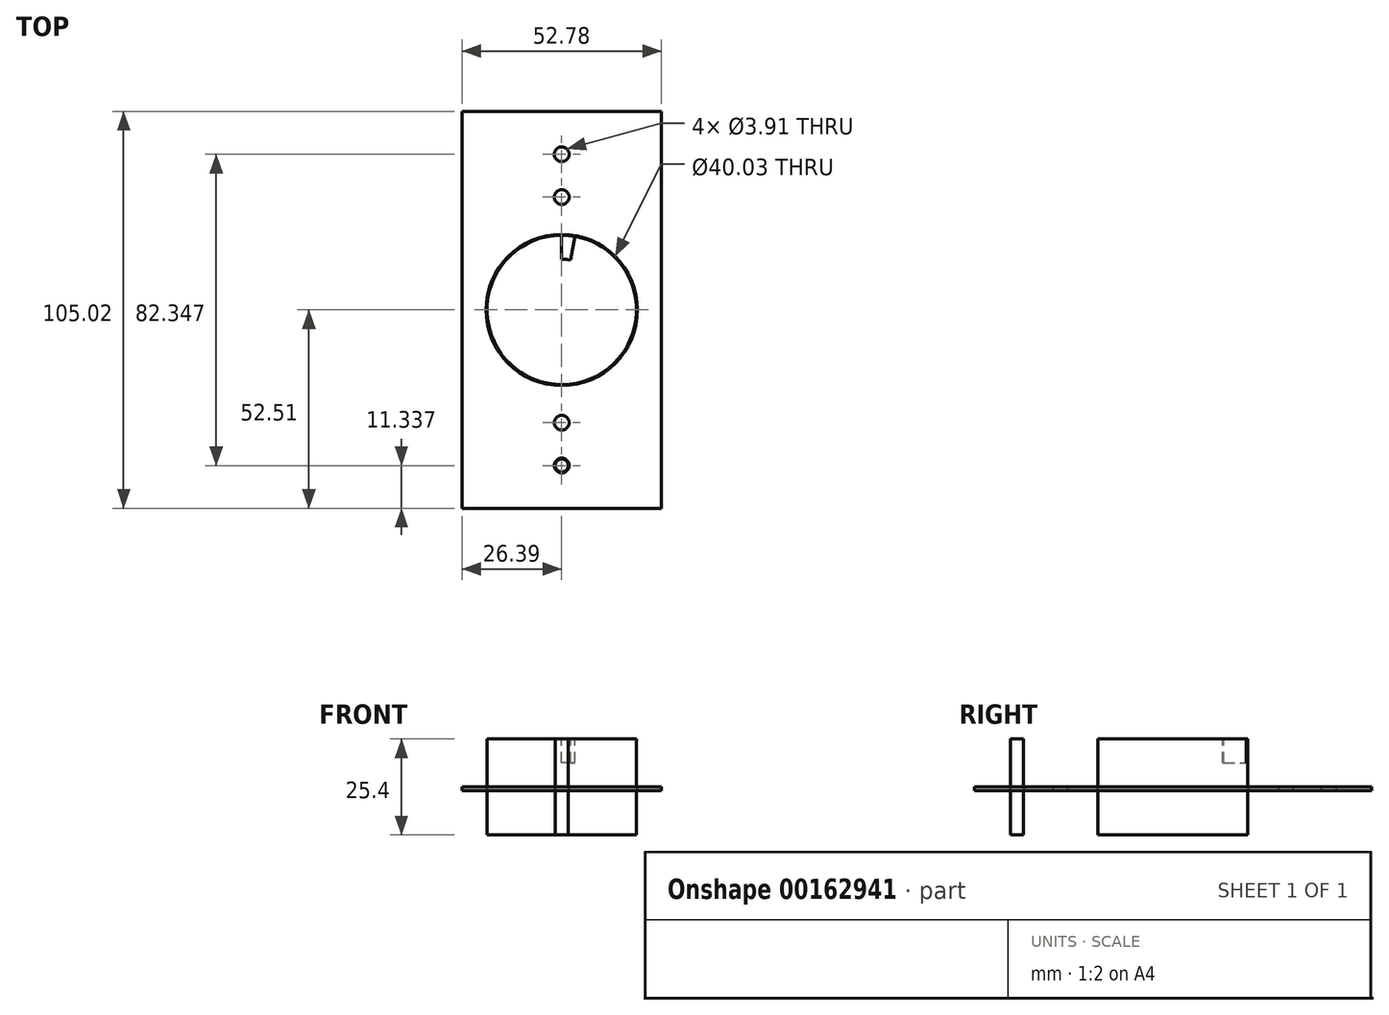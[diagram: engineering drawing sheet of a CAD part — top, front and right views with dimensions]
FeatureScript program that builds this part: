
annotation { "Feature Type Name" : "Feature", "Feature Type Description" : "" }
export const myFeature = defineFeature(function(context is Context, id is Id, definition is map)
    precondition{}
    {
        {
            var Q0;
            Q0=qCreatedBy(makeId("Top.planeOp"),FACE);
            var sketch = newSketch(context, id + "F0", { "sketchPlane" : qUnion([Q0])});
            skLineSegment(sketch, "E0.bottom", {"start": v(-26.4, 52.51) * mm, "end": v(26.4, 52.51) * mm});
            skLineSegment(sketch, "E0.top", {"start": v(-26.4, -52.51) * mm, "end": v(26.4, -52.51) * mm});
            skLineSegment(sketch, "E0.left", {"start": v(-26.4, 52.51) * mm, "end": v(-26.4, -52.51) * mm});
            skLineSegment(sketch, "E0.right", {"start": v(26.4, 52.51) * mm, "end": v(26.4, -52.51) * mm});
            skPoint(sketch, "E1", {"position": v(26.4, 0) * mm});
            skPoint(sketch, "E2", {"position": v(0, 52.51) * mm});
            skCircle(sketch, "E3", {"center": v(0, 0) * mm, "radius": 20.02 * mm});
            skCircle(sketch, "E4", {"center": v(0, 29.85) * mm, "radius": 1.96 * mm});
            skCircle(sketch, "E5", {"center": v(0, 41.17) * mm, "radius": 1.96 * mm});
            skLineSegment(sketch, "E6", {"start": v(26.4, 0) * mm, "end": v(-26.4, 0) * mm, "construction": true});
            skCircle(sketch, "E7.MirrorC", {"center": v(0, -41.17) * mm, "radius": 1.96 * mm});
            skCircle(sketch, "E8.MirrorC", {"center": v(0, -29.85) * mm, "radius": 1.96 * mm});
            skSolve(sketch);
        }
        {
            var Q0;
            Q0=makeQuery(id+"F0.imprint","IMPRINT",FACE,{"disambiguationData":[TD([[makeQuery(id+"F0.imprint","IMPRINT",EDGE,{"derivedFrom":sQuery(id+"F0.wireOp",EDGE,"E0.bottom")}),-1.0]])]});
            extrude(context, id + "F1", {"entities" : qUnion([Q0]), "depth" : 1.04 * mm});
        }
        {
            var Q0;
            Q0=makeQuery(id+"F1.opExtrude","CAP_FACE",FACE,{"disambiguationData":[OSD([sQuery(id+"F0.wireOp",EDGE,"E0.bottom"),sQuery(id+"F0.wireOp",EDGE,"E0.top"),sQuery(id+"F0.wireOp",EDGE,"E0.left"),sQuery(id+"F0.wireOp",EDGE,"E0.right"),sQuery(id+"F0.wireOp",EDGE,"E3"),sQuery(id+"F0.wireOp",EDGE,"E4"),sQuery(id+"F0.wireOp",EDGE,"E5"),sQuery(id+"F0.wireOp",EDGE,"E7.MirrorC"),sQuery(id+"F0.wireOp",EDGE,"E8.MirrorC")])],"isStart":false});
            var sketch = newSketch(context, id + "F2", { "sketchPlane" : qUnion([Q0])});
            skCircle(sketch, "E9", {"center": v(0, 0) * mm, "radius": 19.76 * mm});
            skSolve(sketch);
        }
        {
            var Q0;
            Q0 = qSketchRegion(id + "F2", true);
            extrude(context, id + "F3", {"entities" : qUnion([Q0]), "endBound" : BoundingType.SYMMETRIC, "depth" : 25.4 * mm});
        }
        {
            var Q0;
            Q0=makeQuery(id+"F1.opExtrude","CAP_FACE",FACE,{"disambiguationData":[OSD([sQuery(id+"F0.wireOp",EDGE,"E0.bottom"),sQuery(id+"F0.wireOp",EDGE,"E0.top"),sQuery(id+"F0.wireOp",EDGE,"E0.left"),sQuery(id+"F0.wireOp",EDGE,"E0.right"),sQuery(id+"F0.wireOp",EDGE,"E3"),sQuery(id+"F0.wireOp",EDGE,"E4"),sQuery(id+"F0.wireOp",EDGE,"E5"),sQuery(id+"F0.wireOp",EDGE,"E7.MirrorC"),sQuery(id+"F0.wireOp",EDGE,"E8.MirrorC")])],"isStart":false});
            var sketch = newSketch(context, id + "F4", { "sketchPlane" : qUnion([Q0])});
            skCircle(sketch, "E10", {"center": v(0, -41.17) * mm, "radius": 1.7 * mm});
            skSolve(sketch);
        }
        {
            var Q0;
            Q0=makeQuery(id+"F4.imprint","IMPRINT",FACE,{"disambiguationData":[TD([[makeQuery(id+"F4.imprint","IMPRINT",EDGE,{"derivedFrom":sQuery(id+"F4.wireOp",EDGE,"E10")}),1.0]])]});
            extrude(context, id + "F5", {"entities" : qUnion([Q0]), "endBound" : BoundingType.SYMMETRIC, "depth" : 25.4 * mm});
        }
        {
            var Q0;
            Q0=makeQuery(id+"F3.opExtrude","CAP_FACE",FACE,{"disambiguationData":[OSD([sQuery(id+"F2.wireOp",EDGE,"E9")])],"isStart":false});
            var sketch = newSketch(context, id + "F6", { "sketchPlane" : qUnion([Q0])});
            skCircle(sketch, "E11.0", {"center": v(0, 0) * mm, "radius": 13.41 * mm});
            skLineSegment(sketch, "E12", {"start": v(0, 0) * mm, "end": v(0, 19.76) * mm});
            skLineSegment(sketch, "E13", {"start": v(0, 0) * mm, "end": v(3.43, 19.46) * mm});
            skCircle(sketch, "E14", {"center": v(0, 0) * mm, "radius": 19.76 * mm});
            skSolve(sketch);
        }
        {
            var Q0;
            {var subQ0=sQuery(id+"F6.wireOp",EDGE,"E12");var subQ1=sQuery(id+"F6.wireOp",EDGE,"E11.0");var subQ2=makeQuery(id+"F6.imprint","INTERSECT",VERTEX,{"derivedFrom":[subQ1,subQ0]});Q0=makeQuery(id+"F6.imprint","IMPRINT",FACE,{"disambiguationData":[TD([[makeQuery(id+"F6.imprint","IMPRINT",EDGE,{"disambiguationData":[TD([[subQ2,1.0]])],"derivedFrom":subQ1}),-1.0]])]});}
            extrude(context, id + "F7", {"entities" : qUnion([Q0]), "operationType" : NewBodyOperationType.REMOVE, "oppositeDirection" : true, "depth" : 6.35 * mm});
        }
        {
            var Q0;
            Q0=qCreatedBy(makeId("Front.planeOp"),FACE);
            var sketch = newSketch(context, id + "F8", { "sketchPlane" : qUnion([Q0])});
            skLineSegment(sketch, "E15", {"start": v(0, 0) * mm, "end": v(0, 27.34) * mm});
            skSolve(sketch);
        }
    });
